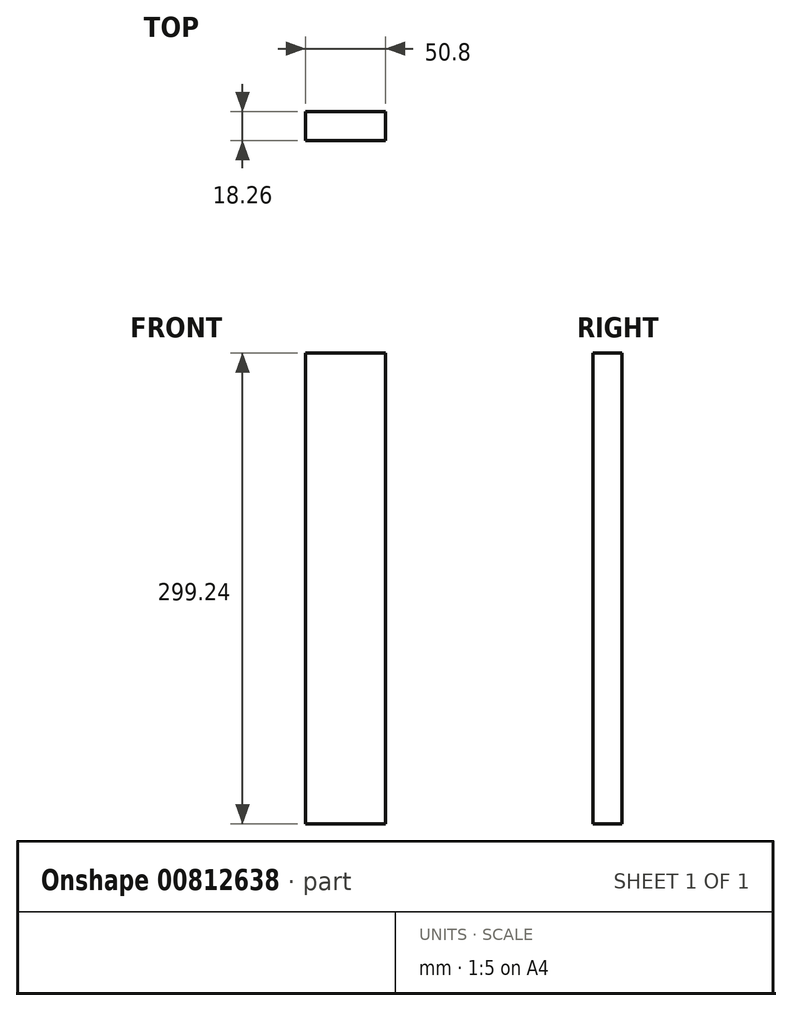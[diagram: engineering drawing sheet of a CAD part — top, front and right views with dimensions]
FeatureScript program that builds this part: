
annotation { "Feature Type Name" : "Feature", "Feature Type Description" : "" }
export const myFeature = defineFeature(function(context is Context, id is Id, definition is map)
    precondition{}
    {
        {
            var Q0;
            Q0=qCreatedBy(makeId("Front.planeOp"),FACE);
            var sketch = newSketch(context, id + "F0", { "sketchPlane" : qUnion([Q0])});
            skLineSegment(sketch, "E0.bottom", {"start": v(25.4, 149.62) * mm, "end": v(-25.4, 149.62) * mm});
            skLineSegment(sketch, "E0.top", {"start": v(25.4, -149.62) * mm, "end": v(-25.4, -149.62) * mm});
            skLineSegment(sketch, "E0.left", {"start": v(25.4, 149.62) * mm, "end": v(25.4, -149.62) * mm});
            skLineSegment(sketch, "E0.right", {"start": v(-25.4, 149.62) * mm, "end": v(-25.4, -149.62) * mm});
            skPoint(sketch, "E0.middle", {"position": v(0, 0) * mm});
            skSolve(sketch);
        }
        {
            var Q0;
            Q0=qSketchRegion(id+"F0",true);
            extrude(context, id + "F1", {"entities" : qUnion([Q0]), "depth" : 18.26 * mm, "offsetDistance" : 25.4 * mm});
        }
    });
